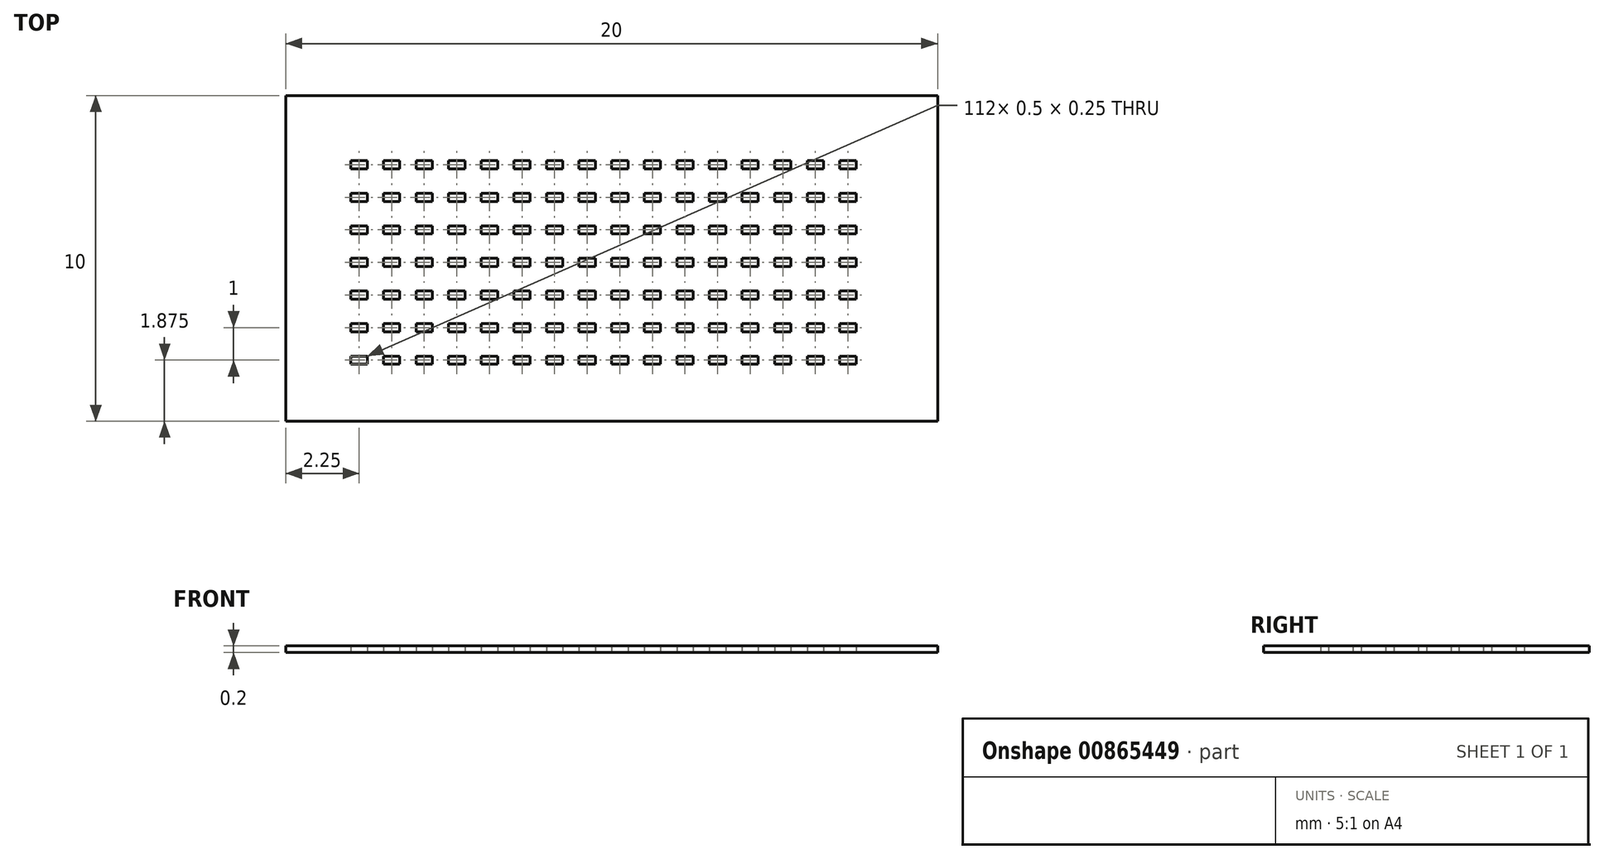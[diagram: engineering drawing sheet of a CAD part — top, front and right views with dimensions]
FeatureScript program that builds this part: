
annotation { "Feature Type Name" : "Feature", "Feature Type Description" : "" }
export const myFeature = defineFeature(function(context is Context, id is Id, definition is map)
    precondition{}
    {
        {
            var Q0;
            Q0=qCreatedBy(makeId("Top.planeOp"),FACE);
            var sketch = newSketch(context, id + "F0", { "sketchPlane" : qUnion([Q0])});
            skLineSegment(sketch, "E0.bottom", {"start": v(0, 0) * mm, "end": v(20, 0) * mm});
            skLineSegment(sketch, "E0.top", {"start": v(0, -10) * mm, "end": v(20, -10) * mm});
            skLineSegment(sketch, "E0.left", {"start": v(0, 0) * mm, "end": v(0, -10) * mm});
            skLineSegment(sketch, "E0.right", {"start": v(20, 0) * mm, "end": v(20, -10) * mm});
            skLineSegment(sketch, "E1.bottom", {"start": v(2, -2) * mm, "end": v(2.5, -2) * mm});
            skLineSegment(sketch, "E1.top", {"start": v(2, -2.25) * mm, "end": v(2.5, -2.25) * mm});
            skLineSegment(sketch, "E1.left", {"start": v(2, -2) * mm, "end": v(2, -2.25) * mm});
            skLineSegment(sketch, "E1.right", {"start": v(2.5, -2) * mm, "end": v(2.5, -2.25) * mm});
            skLineSegment(sketch, "E2.1.0.0", {"start": v(3, -2) * mm, "end": v(3, -2.25) * mm});
            skLineSegment(sketch, "E2.1.0.1", {"start": v(3, -2) * mm, "end": v(3.5, -2) * mm});
            skLineSegment(sketch, "E2.1.0.2", {"start": v(3, -2.25) * mm, "end": v(3.5, -2.25) * mm});
            skLineSegment(sketch, "E2.1.0.3", {"start": v(3.5, -2) * mm, "end": v(3.5, -2.25) * mm});
            skLineSegment(sketch, "E2.2.0.0", {"start": v(4, -2) * mm, "end": v(4, -2.25) * mm});
            skLineSegment(sketch, "E2.2.0.1", {"start": v(4, -2) * mm, "end": v(4.5, -2) * mm});
            skLineSegment(sketch, "E2.2.0.2", {"start": v(4, -2.25) * mm, "end": v(4.5, -2.25) * mm});
            skLineSegment(sketch, "E2.2.0.3", {"start": v(4.5, -2) * mm, "end": v(4.5, -2.25) * mm});
            skLineSegment(sketch, "E2.3.0.0", {"start": v(5, -2) * mm, "end": v(5, -2.25) * mm});
            skLineSegment(sketch, "E2.3.0.1", {"start": v(5, -2) * mm, "end": v(5.5, -2) * mm});
            skLineSegment(sketch, "E2.3.0.2", {"start": v(5, -2.25) * mm, "end": v(5.5, -2.25) * mm});
            skLineSegment(sketch, "E2.3.0.3", {"start": v(5.5, -2) * mm, "end": v(5.5, -2.25) * mm});
            skLineSegment(sketch, "E2.4.0.0", {"start": v(6, -2) * mm, "end": v(6, -2.25) * mm});
            skLineSegment(sketch, "E2.4.0.1", {"start": v(6, -2) * mm, "end": v(6.5, -2) * mm});
            skLineSegment(sketch, "E2.4.0.2", {"start": v(6, -2.25) * mm, "end": v(6.5, -2.25) * mm});
            skLineSegment(sketch, "E2.4.0.3", {"start": v(6.5, -2) * mm, "end": v(6.5, -2.25) * mm});
            skLineSegment(sketch, "E2.5.0.0", {"start": v(7, -2) * mm, "end": v(7, -2.25) * mm});
            skLineSegment(sketch, "E2.5.0.1", {"start": v(7, -2) * mm, "end": v(7.5, -2) * mm});
            skLineSegment(sketch, "E2.5.0.2", {"start": v(7, -2.25) * mm, "end": v(7.5, -2.25) * mm});
            skLineSegment(sketch, "E2.5.0.3", {"start": v(7.5, -2) * mm, "end": v(7.5, -2.25) * mm});
            skLineSegment(sketch, "E2.6.0.0", {"start": v(8, -2) * mm, "end": v(8, -2.25) * mm});
            skLineSegment(sketch, "E2.6.0.1", {"start": v(8, -2) * mm, "end": v(8.5, -2) * mm});
            skLineSegment(sketch, "E2.6.0.2", {"start": v(8, -2.25) * mm, "end": v(8.5, -2.25) * mm});
            skLineSegment(sketch, "E2.6.0.3", {"start": v(8.5, -2) * mm, "end": v(8.5, -2.25) * mm});
            skLineSegment(sketch, "E2.7.0.0", {"start": v(9, -2) * mm, "end": v(9, -2.25) * mm});
            skLineSegment(sketch, "E2.7.0.1", {"start": v(9, -2) * mm, "end": v(9.5, -2) * mm});
            skLineSegment(sketch, "E2.7.0.2", {"start": v(9, -2.25) * mm, "end": v(9.5, -2.25) * mm});
            skLineSegment(sketch, "E2.7.0.3", {"start": v(9.5, -2) * mm, "end": v(9.5, -2.25) * mm});
            skLineSegment(sketch, "E2.8.0.0", {"start": v(10, -2) * mm, "end": v(10, -2.25) * mm});
            skLineSegment(sketch, "E2.8.0.1", {"start": v(10, -2) * mm, "end": v(10.5, -2) * mm});
            skLineSegment(sketch, "E2.8.0.2", {"start": v(10, -2.25) * mm, "end": v(10.5, -2.25) * mm});
            skLineSegment(sketch, "E2.8.0.3", {"start": v(10.5, -2) * mm, "end": v(10.5, -2.25) * mm});
            skLineSegment(sketch, "E2.9.0.0", {"start": v(11, -2) * mm, "end": v(11, -2.25) * mm});
            skLineSegment(sketch, "E2.9.0.1", {"start": v(11, -2) * mm, "end": v(11.5, -2) * mm});
            skLineSegment(sketch, "E2.9.0.2", {"start": v(11, -2.25) * mm, "end": v(11.5, -2.25) * mm});
            skLineSegment(sketch, "E2.9.0.3", {"start": v(11.5, -2) * mm, "end": v(11.5, -2.25) * mm});
            skLineSegment(sketch, "E2.10.0.0", {"start": v(12, -2) * mm, "end": v(12, -2.25) * mm});
            skLineSegment(sketch, "E2.10.0.1", {"start": v(12, -2) * mm, "end": v(12.5, -2) * mm});
            skLineSegment(sketch, "E2.10.0.2", {"start": v(12, -2.25) * mm, "end": v(12.5, -2.25) * mm});
            skLineSegment(sketch, "E2.10.0.3", {"start": v(12.5, -2) * mm, "end": v(12.5, -2.25) * mm});
            skLineSegment(sketch, "E2.11.0.0", {"start": v(13, -2) * mm, "end": v(13, -2.25) * mm});
            skLineSegment(sketch, "E2.11.0.1", {"start": v(13, -2) * mm, "end": v(13.5, -2) * mm});
            skLineSegment(sketch, "E2.11.0.2", {"start": v(13, -2.25) * mm, "end": v(13.5, -2.25) * mm});
            skLineSegment(sketch, "E2.11.0.3", {"start": v(13.5, -2) * mm, "end": v(13.5, -2.25) * mm});
            skLineSegment(sketch, "E2.12.0.0", {"start": v(14, -2) * mm, "end": v(14, -2.25) * mm});
            skLineSegment(sketch, "E2.12.0.1", {"start": v(14, -2) * mm, "end": v(14.5, -2) * mm});
            skLineSegment(sketch, "E2.12.0.2", {"start": v(14, -2.25) * mm, "end": v(14.5, -2.25) * mm});
            skLineSegment(sketch, "E2.12.0.3", {"start": v(14.5, -2) * mm, "end": v(14.5, -2.25) * mm});
            skLineSegment(sketch, "E2.13.0.0", {"start": v(15, -2) * mm, "end": v(15, -2.25) * mm});
            skLineSegment(sketch, "E2.13.0.1", {"start": v(15, -2) * mm, "end": v(15.5, -2) * mm});
            skLineSegment(sketch, "E2.13.0.2", {"start": v(15, -2.25) * mm, "end": v(15.5, -2.25) * mm});
            skLineSegment(sketch, "E2.13.0.3", {"start": v(15.5, -2) * mm, "end": v(15.5, -2.25) * mm});
            skLineSegment(sketch, "E2.14.0.0", {"start": v(16, -2) * mm, "end": v(16, -2.25) * mm});
            skLineSegment(sketch, "E2.14.0.1", {"start": v(16, -2) * mm, "end": v(16.5, -2) * mm});
            skLineSegment(sketch, "E2.14.0.2", {"start": v(16, -2.25) * mm, "end": v(16.5, -2.25) * mm});
            skLineSegment(sketch, "E2.14.0.3", {"start": v(16.5, -2) * mm, "end": v(16.5, -2.25) * mm});
            skLineSegment(sketch, "E2.direction1", {"start": v(2, -2.25) * mm, "end": v(2.5, -2.25) * mm, "construction": true});
            skLineSegment(sketch, "E3.0.15.0", {"start": v(17, -2) * mm, "end": v(17, -2.25) * mm});
            skLineSegment(sketch, "E3.3.15.0", {"start": v(17, -2) * mm, "end": v(17.5, -2) * mm});
            skLineSegment(sketch, "E3.6.15.0", {"start": v(17, -2.25) * mm, "end": v(17.5, -2.25) * mm});
            skLineSegment(sketch, "E3.9.15.0", {"start": v(17.5, -2) * mm, "end": v(17.5, -2.25) * mm});
            skLineSegment(sketch, "E4.1.0.0", {"start": v(5, -3) * mm, "end": v(5.5, -3) * mm});
            skLineSegment(sketch, "E4.1.0.1", {"start": v(9, -3) * mm, "end": v(9.5, -3) * mm});
            skLineSegment(sketch, "E4.1.0.2", {"start": v(13, -3) * mm, "end": v(13.5, -3) * mm});
            skLineSegment(sketch, "E4.1.0.3", {"start": v(15, -3) * mm, "end": v(15, -3.25) * mm});
            skLineSegment(sketch, "E4.1.0.4", {"start": v(7, -3) * mm, "end": v(7, -3.25) * mm});
            skLineSegment(sketch, "E4.1.0.5", {"start": v(5, -3) * mm, "end": v(5, -3.25) * mm});
            skLineSegment(sketch, "E4.1.0.6", {"start": v(13, -3) * mm, "end": v(13, -3.25) * mm});
            skLineSegment(sketch, "E4.1.0.7", {"start": v(10.5, -3) * mm, "end": v(10.5, -3.25) * mm});
            skLineSegment(sketch, "E4.1.0.8", {"start": v(3, -3.25) * mm, "end": v(3.5, -3.25) * mm});
            skLineSegment(sketch, "E4.1.0.9", {"start": v(3, -3) * mm, "end": v(3.5, -3) * mm});
            skLineSegment(sketch, "E4.1.0.10", {"start": v(10, -3.25) * mm, "end": v(10.5, -3.25) * mm});
            skLineSegment(sketch, "E4.1.0.11", {"start": v(14, -3.25) * mm, "end": v(14.5, -3.25) * mm});
            skLineSegment(sketch, "E4.1.0.12", {"start": v(6, -3.25) * mm, "end": v(6.5, -3.25) * mm});
            skLineSegment(sketch, "E4.1.0.13", {"start": v(4, -3.25) * mm, "end": v(4.5, -3.25) * mm});
            skLineSegment(sketch, "E4.1.0.14", {"start": v(4, -3) * mm, "end": v(4.5, -3) * mm});
            skLineSegment(sketch, "E4.1.0.15", {"start": v(4.5, -3) * mm, "end": v(4.5, -3.25) * mm});
            skLineSegment(sketch, "E4.1.0.16", {"start": v(16, -3.25) * mm, "end": v(16.5, -3.25) * mm});
            skLineSegment(sketch, "E4.1.0.17", {"start": v(6, -3) * mm, "end": v(6.5, -3) * mm});
            skLineSegment(sketch, "E4.1.0.18", {"start": v(10, -3) * mm, "end": v(10.5, -3) * mm});
            skLineSegment(sketch, "E4.1.0.19", {"start": v(8, -3.25) * mm, "end": v(8.5, -3.25) * mm});
            skLineSegment(sketch, "E4.1.0.20", {"start": v(12, -3.25) * mm, "end": v(12.5, -3.25) * mm});
            skLineSegment(sketch, "E4.1.0.21", {"start": v(14, -3) * mm, "end": v(14.5, -3) * mm});
            skLineSegment(sketch, "E4.1.0.22", {"start": v(16, -3) * mm, "end": v(16, -3.25) * mm});
            skLineSegment(sketch, "E4.1.0.23", {"start": v(8, -3) * mm, "end": v(8, -3.25) * mm});
            skLineSegment(sketch, "E4.1.0.24", {"start": v(17.5, -3) * mm, "end": v(17.5, -3.25) * mm});
            skLineSegment(sketch, "E4.1.0.25", {"start": v(16, -3) * mm, "end": v(16.5, -3) * mm});
            skLineSegment(sketch, "E4.1.0.26", {"start": v(10, -3) * mm, "end": v(10, -3.25) * mm});
            skLineSegment(sketch, "E4.1.0.27", {"start": v(8, -3) * mm, "end": v(8.5, -3) * mm});
            skLineSegment(sketch, "E4.1.0.28", {"start": v(12, -3) * mm, "end": v(12.5, -3) * mm});
            skLineSegment(sketch, "E4.1.0.29", {"start": v(15.5, -3) * mm, "end": v(15.5, -3.25) * mm});
            skLineSegment(sketch, "E4.1.0.30", {"start": v(7.5, -3) * mm, "end": v(7.5, -3.25) * mm});
            skLineSegment(sketch, "E4.1.0.31", {"start": v(17, -3.25) * mm, "end": v(17.5, -3.25) * mm});
            skLineSegment(sketch, "E4.1.0.32", {"start": v(5.5, -3) * mm, "end": v(5.5, -3.25) * mm});
            skLineSegment(sketch, "E4.1.0.33", {"start": v(12.5, -3) * mm, "end": v(12.5, -3.25) * mm});
            skLineSegment(sketch, "E4.1.0.34", {"start": v(11, -3.25) * mm, "end": v(11.5, -3.25) * mm});
            skLineSegment(sketch, "E4.1.0.35", {"start": v(15, -3.25) * mm, "end": v(15.5, -3.25) * mm});
            skLineSegment(sketch, "E4.1.0.36", {"start": v(7, -3.25) * mm, "end": v(7.5, -3.25) * mm});
            skLineSegment(sketch, "E4.1.0.37", {"start": v(17, -3) * mm, "end": v(17.5, -3) * mm});
            skLineSegment(sketch, "E4.1.0.38", {"start": v(5, -3.25) * mm, "end": v(5.5, -3.25) * mm});
            skLineSegment(sketch, "E4.1.0.39", {"start": v(9, -3.25) * mm, "end": v(9.5, -3.25) * mm});
            skLineSegment(sketch, "E4.1.0.40", {"start": v(13, -3.25) * mm, "end": v(13.5, -3.25) * mm});
            skLineSegment(sketch, "E4.1.0.41", {"start": v(11, -3) * mm, "end": v(11.5, -3) * mm});
            skLineSegment(sketch, "E4.1.0.42", {"start": v(15, -3) * mm, "end": v(15.5, -3) * mm});
            skLineSegment(sketch, "E4.1.0.43", {"start": v(7, -3) * mm, "end": v(7.5, -3) * mm});
            skLineSegment(sketch, "E4.1.0.44", {"start": v(17, -3) * mm, "end": v(17, -3.25) * mm});
            skLineSegment(sketch, "E4.1.0.45", {"start": v(11, -3) * mm, "end": v(11, -3.25) * mm});
            skLineSegment(sketch, "E4.1.0.46", {"start": v(2, -3.25) * mm, "end": v(2.5, -3.25) * mm, "construction": true});
            skLineSegment(sketch, "E4.1.0.47", {"start": v(9, -3) * mm, "end": v(9, -3.25) * mm});
            skLineSegment(sketch, "E4.1.0.48", {"start": v(14.5, -3) * mm, "end": v(14.5, -3.25) * mm});
            skLineSegment(sketch, "E4.1.0.49", {"start": v(6.5, -3) * mm, "end": v(6.5, -3.25) * mm});
            skLineSegment(sketch, "E4.1.0.50", {"start": v(4, -3) * mm, "end": v(4, -3.25) * mm});
            skLineSegment(sketch, "E4.1.0.51", {"start": v(3.5, -3) * mm, "end": v(3.5, -3.25) * mm});
            skLineSegment(sketch, "E4.1.0.52", {"start": v(3, -3) * mm, "end": v(3, -3.25) * mm});
            skLineSegment(sketch, "E4.1.0.53", {"start": v(2.5, -3) * mm, "end": v(2.5, -3.25) * mm});
            skLineSegment(sketch, "E4.1.0.54", {"start": v(2, -3) * mm, "end": v(2, -3.25) * mm});
            skLineSegment(sketch, "E4.1.0.55", {"start": v(2, -3) * mm, "end": v(2.5, -3) * mm});
            skLineSegment(sketch, "E4.1.0.56", {"start": v(12, -3) * mm, "end": v(12, -3.25) * mm});
            skLineSegment(sketch, "E4.1.0.57", {"start": v(6, -3) * mm, "end": v(6, -3.25) * mm});
            skLineSegment(sketch, "E4.1.0.58", {"start": v(14, -3) * mm, "end": v(14, -3.25) * mm});
            skLineSegment(sketch, "E4.1.0.59", {"start": v(11.5, -3) * mm, "end": v(11.5, -3.25) * mm});
            skLineSegment(sketch, "E4.1.0.60", {"start": v(16.5, -3) * mm, "end": v(16.5, -3.25) * mm});
            skLineSegment(sketch, "E4.1.0.61", {"start": v(9.5, -3) * mm, "end": v(9.5, -3.25) * mm});
            skLineSegment(sketch, "E4.1.0.62", {"start": v(8.5, -3) * mm, "end": v(8.5, -3.25) * mm});
            skLineSegment(sketch, "E4.1.0.63", {"start": v(13.5, -3) * mm, "end": v(13.5, -3.25) * mm});
            skLineSegment(sketch, "E4.1.0.64", {"start": v(2, -3.25) * mm, "end": v(2.5, -3.25) * mm});
            skLineSegment(sketch, "E4.2.0.0", {"start": v(5, -4) * mm, "end": v(5.5, -4) * mm});
            skLineSegment(sketch, "E4.2.0.1", {"start": v(9, -4) * mm, "end": v(9.5, -4) * mm});
            skLineSegment(sketch, "E4.2.0.2", {"start": v(13, -4) * mm, "end": v(13.5, -4) * mm});
            skLineSegment(sketch, "E4.2.0.3", {"start": v(15, -4) * mm, "end": v(15, -4.25) * mm});
            skLineSegment(sketch, "E4.2.0.4", {"start": v(7, -4) * mm, "end": v(7, -4.25) * mm});
            skLineSegment(sketch, "E4.2.0.5", {"start": v(5, -4) * mm, "end": v(5, -4.25) * mm});
            skLineSegment(sketch, "E4.2.0.6", {"start": v(13, -4) * mm, "end": v(13, -4.25) * mm});
            skLineSegment(sketch, "E4.2.0.7", {"start": v(10.5, -4) * mm, "end": v(10.5, -4.25) * mm});
            skLineSegment(sketch, "E4.2.0.8", {"start": v(3, -4.25) * mm, "end": v(3.5, -4.25) * mm});
            skLineSegment(sketch, "E4.2.0.9", {"start": v(3, -4) * mm, "end": v(3.5, -4) * mm});
            skLineSegment(sketch, "E4.2.0.10", {"start": v(10, -4.25) * mm, "end": v(10.5, -4.25) * mm});
            skLineSegment(sketch, "E4.2.0.11", {"start": v(14, -4.25) * mm, "end": v(14.5, -4.25) * mm});
            skLineSegment(sketch, "E4.2.0.12", {"start": v(6, -4.25) * mm, "end": v(6.5, -4.25) * mm});
            skLineSegment(sketch, "E4.2.0.13", {"start": v(4, -4.25) * mm, "end": v(4.5, -4.25) * mm});
            skLineSegment(sketch, "E4.2.0.14", {"start": v(4, -4) * mm, "end": v(4.5, -4) * mm});
            skLineSegment(sketch, "E4.2.0.15", {"start": v(4.5, -4) * mm, "end": v(4.5, -4.25) * mm});
            skLineSegment(sketch, "E4.2.0.16", {"start": v(16, -4.25) * mm, "end": v(16.5, -4.25) * mm});
            skLineSegment(sketch, "E4.2.0.17", {"start": v(6, -4) * mm, "end": v(6.5, -4) * mm});
            skLineSegment(sketch, "E4.2.0.18", {"start": v(10, -4) * mm, "end": v(10.5, -4) * mm});
            skLineSegment(sketch, "E4.2.0.19", {"start": v(8, -4.25) * mm, "end": v(8.5, -4.25) * mm});
            skLineSegment(sketch, "E4.2.0.20", {"start": v(12, -4.25) * mm, "end": v(12.5, -4.25) * mm});
            skLineSegment(sketch, "E4.2.0.21", {"start": v(14, -4) * mm, "end": v(14.5, -4) * mm});
            skLineSegment(sketch, "E4.2.0.22", {"start": v(16, -4) * mm, "end": v(16, -4.25) * mm});
            skLineSegment(sketch, "E4.2.0.23", {"start": v(8, -4) * mm, "end": v(8, -4.25) * mm});
            skLineSegment(sketch, "E4.2.0.24", {"start": v(17.5, -4) * mm, "end": v(17.5, -4.25) * mm});
            skLineSegment(sketch, "E4.2.0.25", {"start": v(16, -4) * mm, "end": v(16.5, -4) * mm});
            skLineSegment(sketch, "E4.2.0.26", {"start": v(10, -4) * mm, "end": v(10, -4.25) * mm});
            skLineSegment(sketch, "E4.2.0.27", {"start": v(8, -4) * mm, "end": v(8.5, -4) * mm});
            skLineSegment(sketch, "E4.2.0.28", {"start": v(12, -4) * mm, "end": v(12.5, -4) * mm});
            skLineSegment(sketch, "E4.2.0.29", {"start": v(15.5, -4) * mm, "end": v(15.5, -4.25) * mm});
            skLineSegment(sketch, "E4.2.0.30", {"start": v(7.5, -4) * mm, "end": v(7.5, -4.25) * mm});
            skLineSegment(sketch, "E4.2.0.31", {"start": v(17, -4.25) * mm, "end": v(17.5, -4.25) * mm});
            skLineSegment(sketch, "E4.2.0.32", {"start": v(5.5, -4) * mm, "end": v(5.5, -4.25) * mm});
            skLineSegment(sketch, "E4.2.0.33", {"start": v(12.5, -4) * mm, "end": v(12.5, -4.25) * mm});
            skLineSegment(sketch, "E4.2.0.34", {"start": v(11, -4.25) * mm, "end": v(11.5, -4.25) * mm});
            skLineSegment(sketch, "E4.2.0.35", {"start": v(15, -4.25) * mm, "end": v(15.5, -4.25) * mm});
            skLineSegment(sketch, "E4.2.0.36", {"start": v(7, -4.25) * mm, "end": v(7.5, -4.25) * mm});
            skLineSegment(sketch, "E4.2.0.37", {"start": v(17, -4) * mm, "end": v(17.5, -4) * mm});
            skLineSegment(sketch, "E4.2.0.38", {"start": v(5, -4.25) * mm, "end": v(5.5, -4.25) * mm});
            skLineSegment(sketch, "E4.2.0.39", {"start": v(9, -4.25) * mm, "end": v(9.5, -4.25) * mm});
            skLineSegment(sketch, "E4.2.0.40", {"start": v(13, -4.25) * mm, "end": v(13.5, -4.25) * mm});
            skLineSegment(sketch, "E4.2.0.41", {"start": v(11, -4) * mm, "end": v(11.5, -4) * mm});
            skLineSegment(sketch, "E4.2.0.42", {"start": v(15, -4) * mm, "end": v(15.5, -4) * mm});
            skLineSegment(sketch, "E4.2.0.43", {"start": v(7, -4) * mm, "end": v(7.5, -4) * mm});
            skLineSegment(sketch, "E4.2.0.44", {"start": v(17, -4) * mm, "end": v(17, -4.25) * mm});
            skLineSegment(sketch, "E4.2.0.45", {"start": v(11, -4) * mm, "end": v(11, -4.25) * mm});
            skLineSegment(sketch, "E4.2.0.46", {"start": v(2, -4.25) * mm, "end": v(2.5, -4.25) * mm, "construction": true});
            skLineSegment(sketch, "E4.2.0.47", {"start": v(9, -4) * mm, "end": v(9, -4.25) * mm});
            skLineSegment(sketch, "E4.2.0.48", {"start": v(14.5, -4) * mm, "end": v(14.5, -4.25) * mm});
            skLineSegment(sketch, "E4.2.0.49", {"start": v(6.5, -4) * mm, "end": v(6.5, -4.25) * mm});
            skLineSegment(sketch, "E4.2.0.50", {"start": v(4, -4) * mm, "end": v(4, -4.25) * mm});
            skLineSegment(sketch, "E4.2.0.51", {"start": v(3.5, -4) * mm, "end": v(3.5, -4.25) * mm});
            skLineSegment(sketch, "E4.2.0.52", {"start": v(3, -4) * mm, "end": v(3, -4.25) * mm});
            skLineSegment(sketch, "E4.2.0.53", {"start": v(2.5, -4) * mm, "end": v(2.5, -4.25) * mm});
            skLineSegment(sketch, "E4.2.0.54", {"start": v(2, -4) * mm, "end": v(2, -4.25) * mm});
            skLineSegment(sketch, "E4.2.0.55", {"start": v(2, -4) * mm, "end": v(2.5, -4) * mm});
            skLineSegment(sketch, "E4.2.0.56", {"start": v(12, -4) * mm, "end": v(12, -4.25) * mm});
            skLineSegment(sketch, "E4.2.0.57", {"start": v(6, -4) * mm, "end": v(6, -4.25) * mm});
            skLineSegment(sketch, "E4.2.0.58", {"start": v(14, -4) * mm, "end": v(14, -4.25) * mm});
            skLineSegment(sketch, "E4.2.0.59", {"start": v(11.5, -4) * mm, "end": v(11.5, -4.25) * mm});
            skLineSegment(sketch, "E4.2.0.60", {"start": v(16.5, -4) * mm, "end": v(16.5, -4.25) * mm});
            skLineSegment(sketch, "E4.2.0.61", {"start": v(9.5, -4) * mm, "end": v(9.5, -4.25) * mm});
            skLineSegment(sketch, "E4.2.0.62", {"start": v(8.5, -4) * mm, "end": v(8.5, -4.25) * mm});
            skLineSegment(sketch, "E4.2.0.63", {"start": v(13.5, -4) * mm, "end": v(13.5, -4.25) * mm});
            skLineSegment(sketch, "E4.2.0.64", {"start": v(2, -4.25) * mm, "end": v(2.5, -4.25) * mm});
            skLineSegment(sketch, "E4.3.0.0", {"start": v(5, -5) * mm, "end": v(5.5, -5) * mm});
            skLineSegment(sketch, "E4.3.0.1", {"start": v(9, -5) * mm, "end": v(9.5, -5) * mm});
            skLineSegment(sketch, "E4.3.0.2", {"start": v(13, -5) * mm, "end": v(13.5, -5) * mm});
            skLineSegment(sketch, "E4.3.0.3", {"start": v(15, -5) * mm, "end": v(15, -5.25) * mm});
            skLineSegment(sketch, "E4.3.0.4", {"start": v(7, -5) * mm, "end": v(7, -5.25) * mm});
            skLineSegment(sketch, "E4.3.0.5", {"start": v(5, -5) * mm, "end": v(5, -5.25) * mm});
            skLineSegment(sketch, "E4.3.0.6", {"start": v(13, -5) * mm, "end": v(13, -5.25) * mm});
            skLineSegment(sketch, "E4.3.0.7", {"start": v(10.5, -5) * mm, "end": v(10.5, -5.25) * mm});
            skLineSegment(sketch, "E4.3.0.8", {"start": v(3, -5.25) * mm, "end": v(3.5, -5.25) * mm});
            skLineSegment(sketch, "E4.3.0.9", {"start": v(3, -5) * mm, "end": v(3.5, -5) * mm});
            skLineSegment(sketch, "E4.3.0.10", {"start": v(10, -5.25) * mm, "end": v(10.5, -5.25) * mm});
            skLineSegment(sketch, "E4.3.0.11", {"start": v(14, -5.25) * mm, "end": v(14.5, -5.25) * mm});
            skLineSegment(sketch, "E4.3.0.12", {"start": v(6, -5.25) * mm, "end": v(6.5, -5.25) * mm});
            skLineSegment(sketch, "E4.3.0.13", {"start": v(4, -5.25) * mm, "end": v(4.5, -5.25) * mm});
            skLineSegment(sketch, "E4.3.0.14", {"start": v(4, -5) * mm, "end": v(4.5, -5) * mm});
            skLineSegment(sketch, "E4.3.0.15", {"start": v(4.5, -5) * mm, "end": v(4.5, -5.25) * mm});
            skLineSegment(sketch, "E4.3.0.16", {"start": v(16, -5.25) * mm, "end": v(16.5, -5.25) * mm});
            skLineSegment(sketch, "E4.3.0.17", {"start": v(6, -5) * mm, "end": v(6.5, -5) * mm});
            skLineSegment(sketch, "E4.3.0.18", {"start": v(10, -5) * mm, "end": v(10.5, -5) * mm});
            skLineSegment(sketch, "E4.3.0.19", {"start": v(8, -5.25) * mm, "end": v(8.5, -5.25) * mm});
            skLineSegment(sketch, "E4.3.0.20", {"start": v(12, -5.25) * mm, "end": v(12.5, -5.25) * mm});
            skLineSegment(sketch, "E4.3.0.21", {"start": v(14, -5) * mm, "end": v(14.5, -5) * mm});
            skLineSegment(sketch, "E4.3.0.22", {"start": v(16, -5) * mm, "end": v(16, -5.25) * mm});
            skLineSegment(sketch, "E4.3.0.23", {"start": v(8, -5) * mm, "end": v(8, -5.25) * mm});
            skLineSegment(sketch, "E4.3.0.24", {"start": v(17.5, -5) * mm, "end": v(17.5, -5.25) * mm});
            skLineSegment(sketch, "E4.3.0.25", {"start": v(16, -5) * mm, "end": v(16.5, -5) * mm});
            skLineSegment(sketch, "E4.3.0.26", {"start": v(10, -5) * mm, "end": v(10, -5.25) * mm});
            skLineSegment(sketch, "E4.3.0.27", {"start": v(8, -5) * mm, "end": v(8.5, -5) * mm});
            skLineSegment(sketch, "E4.3.0.28", {"start": v(12, -5) * mm, "end": v(12.5, -5) * mm});
            skLineSegment(sketch, "E4.3.0.29", {"start": v(15.5, -5) * mm, "end": v(15.5, -5.25) * mm});
            skLineSegment(sketch, "E4.3.0.30", {"start": v(7.5, -5) * mm, "end": v(7.5, -5.25) * mm});
            skLineSegment(sketch, "E4.3.0.31", {"start": v(17, -5.25) * mm, "end": v(17.5, -5.25) * mm});
            skLineSegment(sketch, "E4.3.0.32", {"start": v(5.5, -5) * mm, "end": v(5.5, -5.25) * mm});
            skLineSegment(sketch, "E4.3.0.33", {"start": v(12.5, -5) * mm, "end": v(12.5, -5.25) * mm});
            skLineSegment(sketch, "E4.3.0.34", {"start": v(11, -5.25) * mm, "end": v(11.5, -5.25) * mm});
            skLineSegment(sketch, "E4.3.0.35", {"start": v(15, -5.25) * mm, "end": v(15.5, -5.25) * mm});
            skLineSegment(sketch, "E4.3.0.36", {"start": v(7, -5.25) * mm, "end": v(7.5, -5.25) * mm});
            skLineSegment(sketch, "E4.3.0.37", {"start": v(17, -5) * mm, "end": v(17.5, -5) * mm});
            skLineSegment(sketch, "E4.3.0.38", {"start": v(5, -5.25) * mm, "end": v(5.5, -5.25) * mm});
            skLineSegment(sketch, "E4.3.0.39", {"start": v(9, -5.25) * mm, "end": v(9.5, -5.25) * mm});
            skLineSegment(sketch, "E4.3.0.40", {"start": v(13, -5.25) * mm, "end": v(13.5, -5.25) * mm});
            skLineSegment(sketch, "E4.3.0.41", {"start": v(11, -5) * mm, "end": v(11.5, -5) * mm});
            skLineSegment(sketch, "E4.3.0.42", {"start": v(15, -5) * mm, "end": v(15.5, -5) * mm});
            skLineSegment(sketch, "E4.3.0.43", {"start": v(7, -5) * mm, "end": v(7.5, -5) * mm});
            skLineSegment(sketch, "E4.3.0.44", {"start": v(17, -5) * mm, "end": v(17, -5.25) * mm});
            skLineSegment(sketch, "E4.3.0.45", {"start": v(11, -5) * mm, "end": v(11, -5.25) * mm});
            skLineSegment(sketch, "E4.3.0.46", {"start": v(2, -5.25) * mm, "end": v(2.5, -5.25) * mm, "construction": true});
            skLineSegment(sketch, "E4.3.0.47", {"start": v(9, -5) * mm, "end": v(9, -5.25) * mm});
            skLineSegment(sketch, "E4.3.0.48", {"start": v(14.5, -5) * mm, "end": v(14.5, -5.25) * mm});
            skLineSegment(sketch, "E4.3.0.49", {"start": v(6.5, -5) * mm, "end": v(6.5, -5.25) * mm});
            skLineSegment(sketch, "E4.3.0.50", {"start": v(4, -5) * mm, "end": v(4, -5.25) * mm});
            skLineSegment(sketch, "E4.3.0.51", {"start": v(3.5, -5) * mm, "end": v(3.5, -5.25) * mm});
            skLineSegment(sketch, "E4.3.0.52", {"start": v(3, -5) * mm, "end": v(3, -5.25) * mm});
            skLineSegment(sketch, "E4.3.0.53", {"start": v(2.5, -5) * mm, "end": v(2.5, -5.25) * mm});
            skLineSegment(sketch, "E4.3.0.54", {"start": v(2, -5) * mm, "end": v(2, -5.25) * mm});
            skLineSegment(sketch, "E4.3.0.55", {"start": v(2, -5) * mm, "end": v(2.5, -5) * mm});
            skLineSegment(sketch, "E4.3.0.56", {"start": v(12, -5) * mm, "end": v(12, -5.25) * mm});
            skLineSegment(sketch, "E4.3.0.57", {"start": v(6, -5) * mm, "end": v(6, -5.25) * mm});
            skLineSegment(sketch, "E4.3.0.58", {"start": v(14, -5) * mm, "end": v(14, -5.25) * mm});
            skLineSegment(sketch, "E4.3.0.59", {"start": v(11.5, -5) * mm, "end": v(11.5, -5.25) * mm});
            skLineSegment(sketch, "E4.3.0.60", {"start": v(16.5, -5) * mm, "end": v(16.5, -5.25) * mm});
            skLineSegment(sketch, "E4.3.0.61", {"start": v(9.5, -5) * mm, "end": v(9.5, -5.25) * mm});
            skLineSegment(sketch, "E4.3.0.62", {"start": v(8.5, -5) * mm, "end": v(8.5, -5.25) * mm});
            skLineSegment(sketch, "E4.3.0.63", {"start": v(13.5, -5) * mm, "end": v(13.5, -5.25) * mm});
            skLineSegment(sketch, "E4.3.0.64", {"start": v(2, -5.25) * mm, "end": v(2.5, -5.25) * mm});
            skLineSegment(sketch, "E4.4.0.0", {"start": v(5, -6) * mm, "end": v(5.5, -6) * mm});
            skLineSegment(sketch, "E4.4.0.1", {"start": v(9, -6) * mm, "end": v(9.5, -6) * mm});
            skLineSegment(sketch, "E4.4.0.2", {"start": v(13, -6) * mm, "end": v(13.5, -6) * mm});
            skLineSegment(sketch, "E4.4.0.3", {"start": v(15, -6) * mm, "end": v(15, -6.25) * mm});
            skLineSegment(sketch, "E4.4.0.4", {"start": v(7, -6) * mm, "end": v(7, -6.25) * mm});
            skLineSegment(sketch, "E4.4.0.5", {"start": v(5, -6) * mm, "end": v(5, -6.25) * mm});
            skLineSegment(sketch, "E4.4.0.6", {"start": v(13, -6) * mm, "end": v(13, -6.25) * mm});
            skLineSegment(sketch, "E4.4.0.7", {"start": v(10.5, -6) * mm, "end": v(10.5, -6.25) * mm});
            skLineSegment(sketch, "E4.4.0.8", {"start": v(3, -6.25) * mm, "end": v(3.5, -6.25) * mm});
            skLineSegment(sketch, "E4.4.0.9", {"start": v(3, -6) * mm, "end": v(3.5, -6) * mm});
            skLineSegment(sketch, "E4.4.0.10", {"start": v(10, -6.25) * mm, "end": v(10.5, -6.25) * mm});
            skLineSegment(sketch, "E4.4.0.11", {"start": v(14, -6.25) * mm, "end": v(14.5, -6.25) * mm});
            skLineSegment(sketch, "E4.4.0.12", {"start": v(6, -6.25) * mm, "end": v(6.5, -6.25) * mm});
            skLineSegment(sketch, "E4.4.0.13", {"start": v(4, -6.25) * mm, "end": v(4.5, -6.25) * mm});
            skLineSegment(sketch, "E4.4.0.14", {"start": v(4, -6) * mm, "end": v(4.5, -6) * mm});
            skLineSegment(sketch, "E4.4.0.15", {"start": v(4.5, -6) * mm, "end": v(4.5, -6.25) * mm});
            skLineSegment(sketch, "E4.4.0.16", {"start": v(16, -6.25) * mm, "end": v(16.5, -6.25) * mm});
            skLineSegment(sketch, "E4.4.0.17", {"start": v(6, -6) * mm, "end": v(6.5, -6) * mm});
            skLineSegment(sketch, "E4.4.0.18", {"start": v(10, -6) * mm, "end": v(10.5, -6) * mm});
            skLineSegment(sketch, "E4.4.0.19", {"start": v(8, -6.25) * mm, "end": v(8.5, -6.25) * mm});
            skLineSegment(sketch, "E4.4.0.20", {"start": v(12, -6.25) * mm, "end": v(12.5, -6.25) * mm});
            skLineSegment(sketch, "E4.4.0.21", {"start": v(14, -6) * mm, "end": v(14.5, -6) * mm});
            skLineSegment(sketch, "E4.4.0.22", {"start": v(16, -6) * mm, "end": v(16, -6.25) * mm});
            skLineSegment(sketch, "E4.4.0.23", {"start": v(8, -6) * mm, "end": v(8, -6.25) * mm});
            skLineSegment(sketch, "E4.4.0.24", {"start": v(17.5, -6) * mm, "end": v(17.5, -6.25) * mm});
            skLineSegment(sketch, "E4.4.0.25", {"start": v(16, -6) * mm, "end": v(16.5, -6) * mm});
            skLineSegment(sketch, "E4.4.0.26", {"start": v(10, -6) * mm, "end": v(10, -6.25) * mm});
            skLineSegment(sketch, "E4.4.0.27", {"start": v(8, -6) * mm, "end": v(8.5, -6) * mm});
            skLineSegment(sketch, "E4.4.0.28", {"start": v(12, -6) * mm, "end": v(12.5, -6) * mm});
            skLineSegment(sketch, "E4.4.0.29", {"start": v(15.5, -6) * mm, "end": v(15.5, -6.25) * mm});
            skLineSegment(sketch, "E4.4.0.30", {"start": v(7.5, -6) * mm, "end": v(7.5, -6.25) * mm});
            skLineSegment(sketch, "E4.4.0.31", {"start": v(17, -6.25) * mm, "end": v(17.5, -6.25) * mm});
            skLineSegment(sketch, "E4.4.0.32", {"start": v(5.5, -6) * mm, "end": v(5.5, -6.25) * mm});
            skLineSegment(sketch, "E4.4.0.33", {"start": v(12.5, -6) * mm, "end": v(12.5, -6.25) * mm});
            skLineSegment(sketch, "E4.4.0.34", {"start": v(11, -6.25) * mm, "end": v(11.5, -6.25) * mm});
            skLineSegment(sketch, "E4.4.0.35", {"start": v(15, -6.25) * mm, "end": v(15.5, -6.25) * mm});
            skLineSegment(sketch, "E4.4.0.36", {"start": v(7, -6.25) * mm, "end": v(7.5, -6.25) * mm});
            skLineSegment(sketch, "E4.4.0.37", {"start": v(17, -6) * mm, "end": v(17.5, -6) * mm});
            skLineSegment(sketch, "E4.4.0.38", {"start": v(5, -6.25) * mm, "end": v(5.5, -6.25) * mm});
            skLineSegment(sketch, "E4.4.0.39", {"start": v(9, -6.25) * mm, "end": v(9.5, -6.25) * mm});
            skLineSegment(sketch, "E4.4.0.40", {"start": v(13, -6.25) * mm, "end": v(13.5, -6.25) * mm});
            skLineSegment(sketch, "E4.4.0.41", {"start": v(11, -6) * mm, "end": v(11.5, -6) * mm});
            skLineSegment(sketch, "E4.4.0.42", {"start": v(15, -6) * mm, "end": v(15.5, -6) * mm});
            skLineSegment(sketch, "E4.4.0.43", {"start": v(7, -6) * mm, "end": v(7.5, -6) * mm});
            skLineSegment(sketch, "E4.4.0.44", {"start": v(17, -6) * mm, "end": v(17, -6.25) * mm});
            skLineSegment(sketch, "E4.4.0.45", {"start": v(11, -6) * mm, "end": v(11, -6.25) * mm});
            skLineSegment(sketch, "E4.4.0.46", {"start": v(2, -6.25) * mm, "end": v(2.5, -6.25) * mm, "construction": true});
            skLineSegment(sketch, "E4.4.0.47", {"start": v(9, -6) * mm, "end": v(9, -6.25) * mm});
            skLineSegment(sketch, "E4.4.0.48", {"start": v(14.5, -6) * mm, "end": v(14.5, -6.25) * mm});
            skLineSegment(sketch, "E4.4.0.49", {"start": v(6.5, -6) * mm, "end": v(6.5, -6.25) * mm});
            skLineSegment(sketch, "E4.4.0.50", {"start": v(4, -6) * mm, "end": v(4, -6.25) * mm});
            skLineSegment(sketch, "E4.4.0.51", {"start": v(3.5, -6) * mm, "end": v(3.5, -6.25) * mm});
            skLineSegment(sketch, "E4.4.0.52", {"start": v(3, -6) * mm, "end": v(3, -6.25) * mm});
            skLineSegment(sketch, "E4.4.0.53", {"start": v(2.5, -6) * mm, "end": v(2.5, -6.25) * mm});
            skLineSegment(sketch, "E4.4.0.54", {"start": v(2, -6) * mm, "end": v(2, -6.25) * mm});
            skLineSegment(sketch, "E4.4.0.55", {"start": v(2, -6) * mm, "end": v(2.5, -6) * mm});
            skLineSegment(sketch, "E4.4.0.56", {"start": v(12, -6) * mm, "end": v(12, -6.25) * mm});
            skLineSegment(sketch, "E4.4.0.57", {"start": v(6, -6) * mm, "end": v(6, -6.25) * mm});
            skLineSegment(sketch, "E4.4.0.58", {"start": v(14, -6) * mm, "end": v(14, -6.25) * mm});
            skLineSegment(sketch, "E4.4.0.59", {"start": v(11.5, -6) * mm, "end": v(11.5, -6.25) * mm});
            skLineSegment(sketch, "E4.4.0.60", {"start": v(16.5, -6) * mm, "end": v(16.5, -6.25) * mm});
            skLineSegment(sketch, "E4.4.0.61", {"start": v(9.5, -6) * mm, "end": v(9.5, -6.25) * mm});
            skLineSegment(sketch, "E4.4.0.62", {"start": v(8.5, -6) * mm, "end": v(8.5, -6.25) * mm});
            skLineSegment(sketch, "E4.4.0.63", {"start": v(13.5, -6) * mm, "end": v(13.5, -6.25) * mm});
            skLineSegment(sketch, "E4.4.0.64", {"start": v(2, -6.25) * mm, "end": v(2.5, -6.25) * mm});
            skLineSegment(sketch, "E4.5.0.0", {"start": v(5, -7) * mm, "end": v(5.5, -7) * mm});
            skLineSegment(sketch, "E4.5.0.1", {"start": v(9, -7) * mm, "end": v(9.5, -7) * mm});
            skLineSegment(sketch, "E4.5.0.2", {"start": v(13, -7) * mm, "end": v(13.5, -7) * mm});
            skLineSegment(sketch, "E4.5.0.3", {"start": v(15, -7) * mm, "end": v(15, -7.25) * mm});
            skLineSegment(sketch, "E4.5.0.4", {"start": v(7, -7) * mm, "end": v(7, -7.25) * mm});
            skLineSegment(sketch, "E4.5.0.5", {"start": v(5, -7) * mm, "end": v(5, -7.25) * mm});
            skLineSegment(sketch, "E4.5.0.6", {"start": v(13, -7) * mm, "end": v(13, -7.25) * mm});
            skLineSegment(sketch, "E4.5.0.7", {"start": v(10.5, -7) * mm, "end": v(10.5, -7.25) * mm});
            skLineSegment(sketch, "E4.5.0.8", {"start": v(3, -7.25) * mm, "end": v(3.5, -7.25) * mm});
            skLineSegment(sketch, "E4.5.0.9", {"start": v(3, -7) * mm, "end": v(3.5, -7) * mm});
            skLineSegment(sketch, "E4.5.0.10", {"start": v(10, -7.25) * mm, "end": v(10.5, -7.25) * mm});
            skLineSegment(sketch, "E4.5.0.11", {"start": v(14, -7.25) * mm, "end": v(14.5, -7.25) * mm});
            skLineSegment(sketch, "E4.5.0.12", {"start": v(6, -7.25) * mm, "end": v(6.5, -7.25) * mm});
            skLineSegment(sketch, "E4.5.0.13", {"start": v(4, -7.25) * mm, "end": v(4.5, -7.25) * mm});
            skLineSegment(sketch, "E4.5.0.14", {"start": v(4, -7) * mm, "end": v(4.5, -7) * mm});
            skLineSegment(sketch, "E4.5.0.15", {"start": v(4.5, -7) * mm, "end": v(4.5, -7.25) * mm});
            skLineSegment(sketch, "E4.5.0.16", {"start": v(16, -7.25) * mm, "end": v(16.5, -7.25) * mm});
            skLineSegment(sketch, "E4.5.0.17", {"start": v(6, -7) * mm, "end": v(6.5, -7) * mm});
            skLineSegment(sketch, "E4.5.0.18", {"start": v(10, -7) * mm, "end": v(10.5, -7) * mm});
            skLineSegment(sketch, "E4.5.0.19", {"start": v(8, -7.25) * mm, "end": v(8.5, -7.25) * mm});
            skLineSegment(sketch, "E4.5.0.20", {"start": v(12, -7.25) * mm, "end": v(12.5, -7.25) * mm});
            skLineSegment(sketch, "E4.5.0.21", {"start": v(14, -7) * mm, "end": v(14.5, -7) * mm});
            skLineSegment(sketch, "E4.5.0.22", {"start": v(16, -7) * mm, "end": v(16, -7.25) * mm});
            skLineSegment(sketch, "E4.5.0.23", {"start": v(8, -7) * mm, "end": v(8, -7.25) * mm});
            skLineSegment(sketch, "E4.5.0.24", {"start": v(17.5, -7) * mm, "end": v(17.5, -7.25) * mm});
            skLineSegment(sketch, "E4.5.0.25", {"start": v(16, -7) * mm, "end": v(16.5, -7) * mm});
            skLineSegment(sketch, "E4.5.0.26", {"start": v(10, -7) * mm, "end": v(10, -7.25) * mm});
            skLineSegment(sketch, "E4.5.0.27", {"start": v(8, -7) * mm, "end": v(8.5, -7) * mm});
            skLineSegment(sketch, "E4.5.0.28", {"start": v(12, -7) * mm, "end": v(12.5, -7) * mm});
            skLineSegment(sketch, "E4.5.0.29", {"start": v(15.5, -7) * mm, "end": v(15.5, -7.25) * mm});
            skLineSegment(sketch, "E4.5.0.30", {"start": v(7.5, -7) * mm, "end": v(7.5, -7.25) * mm});
            skLineSegment(sketch, "E4.5.0.31", {"start": v(17, -7.25) * mm, "end": v(17.5, -7.25) * mm});
            skLineSegment(sketch, "E4.5.0.32", {"start": v(5.5, -7) * mm, "end": v(5.5, -7.25) * mm});
            skLineSegment(sketch, "E4.5.0.33", {"start": v(12.5, -7) * mm, "end": v(12.5, -7.25) * mm});
            skLineSegment(sketch, "E4.5.0.34", {"start": v(11, -7.25) * mm, "end": v(11.5, -7.25) * mm});
            skLineSegment(sketch, "E4.5.0.35", {"start": v(15, -7.25) * mm, "end": v(15.5, -7.25) * mm});
            skLineSegment(sketch, "E4.5.0.36", {"start": v(7, -7.25) * mm, "end": v(7.5, -7.25) * mm});
            skLineSegment(sketch, "E4.5.0.37", {"start": v(17, -7) * mm, "end": v(17.5, -7) * mm});
            skLineSegment(sketch, "E4.5.0.38", {"start": v(5, -7.25) * mm, "end": v(5.5, -7.25) * mm});
            skLineSegment(sketch, "E4.5.0.39", {"start": v(9, -7.25) * mm, "end": v(9.5, -7.25) * mm});
            skLineSegment(sketch, "E4.5.0.40", {"start": v(13, -7.25) * mm, "end": v(13.5, -7.25) * mm});
            skLineSegment(sketch, "E4.5.0.41", {"start": v(11, -7) * mm, "end": v(11.5, -7) * mm});
            skLineSegment(sketch, "E4.5.0.42", {"start": v(15, -7) * mm, "end": v(15.5, -7) * mm});
            skLineSegment(sketch, "E4.5.0.43", {"start": v(7, -7) * mm, "end": v(7.5, -7) * mm});
            skLineSegment(sketch, "E4.5.0.44", {"start": v(17, -7) * mm, "end": v(17, -7.25) * mm});
            skLineSegment(sketch, "E4.5.0.45", {"start": v(11, -7) * mm, "end": v(11, -7.25) * mm});
            skLineSegment(sketch, "E4.5.0.46", {"start": v(2, -7.25) * mm, "end": v(2.5, -7.25) * mm, "construction": true});
            skLineSegment(sketch, "E4.5.0.47", {"start": v(9, -7) * mm, "end": v(9, -7.25) * mm});
            skLineSegment(sketch, "E4.5.0.48", {"start": v(14.5, -7) * mm, "end": v(14.5, -7.25) * mm});
            skLineSegment(sketch, "E4.5.0.49", {"start": v(6.5, -7) * mm, "end": v(6.5, -7.25) * mm});
            skLineSegment(sketch, "E4.5.0.50", {"start": v(4, -7) * mm, "end": v(4, -7.25) * mm});
            skLineSegment(sketch, "E4.5.0.51", {"start": v(3.5, -7) * mm, "end": v(3.5, -7.25) * mm});
            skLineSegment(sketch, "E4.5.0.52", {"start": v(3, -7) * mm, "end": v(3, -7.25) * mm});
            skLineSegment(sketch, "E4.5.0.53", {"start": v(2.5, -7) * mm, "end": v(2.5, -7.25) * mm});
            skLineSegment(sketch, "E4.5.0.54", {"start": v(2, -7) * mm, "end": v(2, -7.25) * mm});
            skLineSegment(sketch, "E4.5.0.55", {"start": v(2, -7) * mm, "end": v(2.5, -7) * mm});
            skLineSegment(sketch, "E4.5.0.56", {"start": v(12, -7) * mm, "end": v(12, -7.25) * mm});
            skLineSegment(sketch, "E4.5.0.57", {"start": v(6, -7) * mm, "end": v(6, -7.25) * mm});
            skLineSegment(sketch, "E4.5.0.58", {"start": v(14, -7) * mm, "end": v(14, -7.25) * mm});
            skLineSegment(sketch, "E4.5.0.59", {"start": v(11.5, -7) * mm, "end": v(11.5, -7.25) * mm});
            skLineSegment(sketch, "E4.5.0.60", {"start": v(16.5, -7) * mm, "end": v(16.5, -7.25) * mm});
            skLineSegment(sketch, "E4.5.0.61", {"start": v(9.5, -7) * mm, "end": v(9.5, -7.25) * mm});
            skLineSegment(sketch, "E4.5.0.62", {"start": v(8.5, -7) * mm, "end": v(8.5, -7.25) * mm});
            skLineSegment(sketch, "E4.5.0.63", {"start": v(13.5, -7) * mm, "end": v(13.5, -7.25) * mm});
            skLineSegment(sketch, "E4.5.0.64", {"start": v(2, -7.25) * mm, "end": v(2.5, -7.25) * mm});
            skLineSegment(sketch, "E4.6.0.0", {"start": v(5, -8) * mm, "end": v(5.5, -8) * mm});
            skLineSegment(sketch, "E4.6.0.1", {"start": v(9, -8) * mm, "end": v(9.5, -8) * mm});
            skLineSegment(sketch, "E4.6.0.2", {"start": v(13, -8) * mm, "end": v(13.5, -8) * mm});
            skLineSegment(sketch, "E4.6.0.3", {"start": v(15, -8) * mm, "end": v(15, -8.25) * mm});
            skLineSegment(sketch, "E4.6.0.4", {"start": v(7, -8) * mm, "end": v(7, -8.25) * mm});
            skLineSegment(sketch, "E4.6.0.5", {"start": v(5, -8) * mm, "end": v(5, -8.25) * mm});
            skLineSegment(sketch, "E4.6.0.6", {"start": v(13, -8) * mm, "end": v(13, -8.25) * mm});
            skLineSegment(sketch, "E4.6.0.7", {"start": v(10.5, -8) * mm, "end": v(10.5, -8.25) * mm});
            skLineSegment(sketch, "E4.6.0.8", {"start": v(3, -8.25) * mm, "end": v(3.5, -8.25) * mm});
            skLineSegment(sketch, "E4.6.0.9", {"start": v(3, -8) * mm, "end": v(3.5, -8) * mm});
            skLineSegment(sketch, "E4.6.0.10", {"start": v(10, -8.25) * mm, "end": v(10.5, -8.25) * mm});
            skLineSegment(sketch, "E4.6.0.11", {"start": v(14, -8.25) * mm, "end": v(14.5, -8.25) * mm});
            skLineSegment(sketch, "E4.6.0.12", {"start": v(6, -8.25) * mm, "end": v(6.5, -8.25) * mm});
            skLineSegment(sketch, "E4.6.0.13", {"start": v(4, -8.25) * mm, "end": v(4.5, -8.25) * mm});
            skLineSegment(sketch, "E4.6.0.14", {"start": v(4, -8) * mm, "end": v(4.5, -8) * mm});
            skLineSegment(sketch, "E4.6.0.15", {"start": v(4.5, -8) * mm, "end": v(4.5, -8.25) * mm});
            skLineSegment(sketch, "E4.6.0.16", {"start": v(16, -8.25) * mm, "end": v(16.5, -8.25) * mm});
            skLineSegment(sketch, "E4.6.0.17", {"start": v(6, -8) * mm, "end": v(6.5, -8) * mm});
            skLineSegment(sketch, "E4.6.0.18", {"start": v(10, -8) * mm, "end": v(10.5, -8) * mm});
            skLineSegment(sketch, "E4.6.0.19", {"start": v(8, -8.25) * mm, "end": v(8.5, -8.25) * mm});
            skLineSegment(sketch, "E4.6.0.20", {"start": v(12, -8.25) * mm, "end": v(12.5, -8.25) * mm});
            skLineSegment(sketch, "E4.6.0.21", {"start": v(14, -8) * mm, "end": v(14.5, -8) * mm});
            skLineSegment(sketch, "E4.6.0.22", {"start": v(16, -8) * mm, "end": v(16, -8.25) * mm});
            skLineSegment(sketch, "E4.6.0.23", {"start": v(8, -8) * mm, "end": v(8, -8.25) * mm});
            skLineSegment(sketch, "E4.6.0.24", {"start": v(17.5, -8) * mm, "end": v(17.5, -8.25) * mm});
            skLineSegment(sketch, "E4.6.0.25", {"start": v(16, -8) * mm, "end": v(16.5, -8) * mm});
            skLineSegment(sketch, "E4.6.0.26", {"start": v(10, -8) * mm, "end": v(10, -8.25) * mm});
            skLineSegment(sketch, "E4.6.0.27", {"start": v(8, -8) * mm, "end": v(8.5, -8) * mm});
            skLineSegment(sketch, "E4.6.0.28", {"start": v(12, -8) * mm, "end": v(12.5, -8) * mm});
            skLineSegment(sketch, "E4.6.0.29", {"start": v(15.5, -8) * mm, "end": v(15.5, -8.25) * mm});
            skLineSegment(sketch, "E4.6.0.30", {"start": v(7.5, -8) * mm, "end": v(7.5, -8.25) * mm});
            skLineSegment(sketch, "E4.6.0.31", {"start": v(17, -8.25) * mm, "end": v(17.5, -8.25) * mm});
            skLineSegment(sketch, "E4.6.0.32", {"start": v(5.5, -8) * mm, "end": v(5.5, -8.25) * mm});
            skLineSegment(sketch, "E4.6.0.33", {"start": v(12.5, -8) * mm, "end": v(12.5, -8.25) * mm});
            skLineSegment(sketch, "E4.6.0.34", {"start": v(11, -8.25) * mm, "end": v(11.5, -8.25) * mm});
            skLineSegment(sketch, "E4.6.0.35", {"start": v(15, -8.25) * mm, "end": v(15.5, -8.25) * mm});
            skLineSegment(sketch, "E4.6.0.36", {"start": v(7, -8.25) * mm, "end": v(7.5, -8.25) * mm});
            skLineSegment(sketch, "E4.6.0.37", {"start": v(17, -8) * mm, "end": v(17.5, -8) * mm});
            skLineSegment(sketch, "E4.6.0.38", {"start": v(5, -8.25) * mm, "end": v(5.5, -8.25) * mm});
            skLineSegment(sketch, "E4.6.0.39", {"start": v(9, -8.25) * mm, "end": v(9.5, -8.25) * mm});
            skLineSegment(sketch, "E4.6.0.40", {"start": v(13, -8.25) * mm, "end": v(13.5, -8.25) * mm});
            skLineSegment(sketch, "E4.6.0.41", {"start": v(11, -8) * mm, "end": v(11.5, -8) * mm});
            skLineSegment(sketch, "E4.6.0.42", {"start": v(15, -8) * mm, "end": v(15.5, -8) * mm});
            skLineSegment(sketch, "E4.6.0.43", {"start": v(7, -8) * mm, "end": v(7.5, -8) * mm});
            skLineSegment(sketch, "E4.6.0.44", {"start": v(17, -8) * mm, "end": v(17, -8.25) * mm});
            skLineSegment(sketch, "E4.6.0.45", {"start": v(11, -8) * mm, "end": v(11, -8.25) * mm});
            skLineSegment(sketch, "E4.6.0.46", {"start": v(2, -8.25) * mm, "end": v(2.5, -8.25) * mm, "construction": true});
            skLineSegment(sketch, "E4.6.0.47", {"start": v(9, -8) * mm, "end": v(9, -8.25) * mm});
            skLineSegment(sketch, "E4.6.0.48", {"start": v(14.5, -8) * mm, "end": v(14.5, -8.25) * mm});
            skLineSegment(sketch, "E4.6.0.49", {"start": v(6.5, -8) * mm, "end": v(6.5, -8.25) * mm});
            skLineSegment(sketch, "E4.6.0.50", {"start": v(4, -8) * mm, "end": v(4, -8.25) * mm});
            skLineSegment(sketch, "E4.6.0.51", {"start": v(3.5, -8) * mm, "end": v(3.5, -8.25) * mm});
            skLineSegment(sketch, "E4.6.0.52", {"start": v(3, -8) * mm, "end": v(3, -8.25) * mm});
            skLineSegment(sketch, "E4.6.0.53", {"start": v(2.5, -8) * mm, "end": v(2.5, -8.25) * mm});
            skLineSegment(sketch, "E4.6.0.54", {"start": v(2, -8) * mm, "end": v(2, -8.25) * mm});
            skLineSegment(sketch, "E4.6.0.55", {"start": v(2, -8) * mm, "end": v(2.5, -8) * mm});
            skLineSegment(sketch, "E4.6.0.56", {"start": v(12, -8) * mm, "end": v(12, -8.25) * mm});
            skLineSegment(sketch, "E4.6.0.57", {"start": v(6, -8) * mm, "end": v(6, -8.25) * mm});
            skLineSegment(sketch, "E4.6.0.58", {"start": v(14, -8) * mm, "end": v(14, -8.25) * mm});
            skLineSegment(sketch, "E4.6.0.59", {"start": v(11.5, -8) * mm, "end": v(11.5, -8.25) * mm});
            skLineSegment(sketch, "E4.6.0.60", {"start": v(16.5, -8) * mm, "end": v(16.5, -8.25) * mm});
            skLineSegment(sketch, "E4.6.0.61", {"start": v(9.5, -8) * mm, "end": v(9.5, -8.25) * mm});
            skLineSegment(sketch, "E4.6.0.62", {"start": v(8.5, -8) * mm, "end": v(8.5, -8.25) * mm});
            skLineSegment(sketch, "E4.6.0.63", {"start": v(13.5, -8) * mm, "end": v(13.5, -8.25) * mm});
            skLineSegment(sketch, "E4.6.0.64", {"start": v(2, -8.25) * mm, "end": v(2.5, -8.25) * mm});
            skLineSegment(sketch, "E4.direction1", {"start": v(2, -2.25) * mm, "end": v(2, -3.25) * mm, "construction": true});
            skSolve(sketch);
        }
        {
            var Q0;
            Q0=makeQuery(id+"F0.imprint","IMPRINT",FACE,{"disambiguationData":[TD([[makeQuery(id+"F0.imprint","IMPRINT",EDGE,{"derivedFrom":sQuery(id+"F0.wireOp",EDGE,"E0.bottom")}),-1.0]])]});
            extrude(context, id + "F1", {"entities" : qUnion([Q0]), "depth" : 0.2 * mm, "offsetDistance" : 25.4 * mm});
        }
    });
